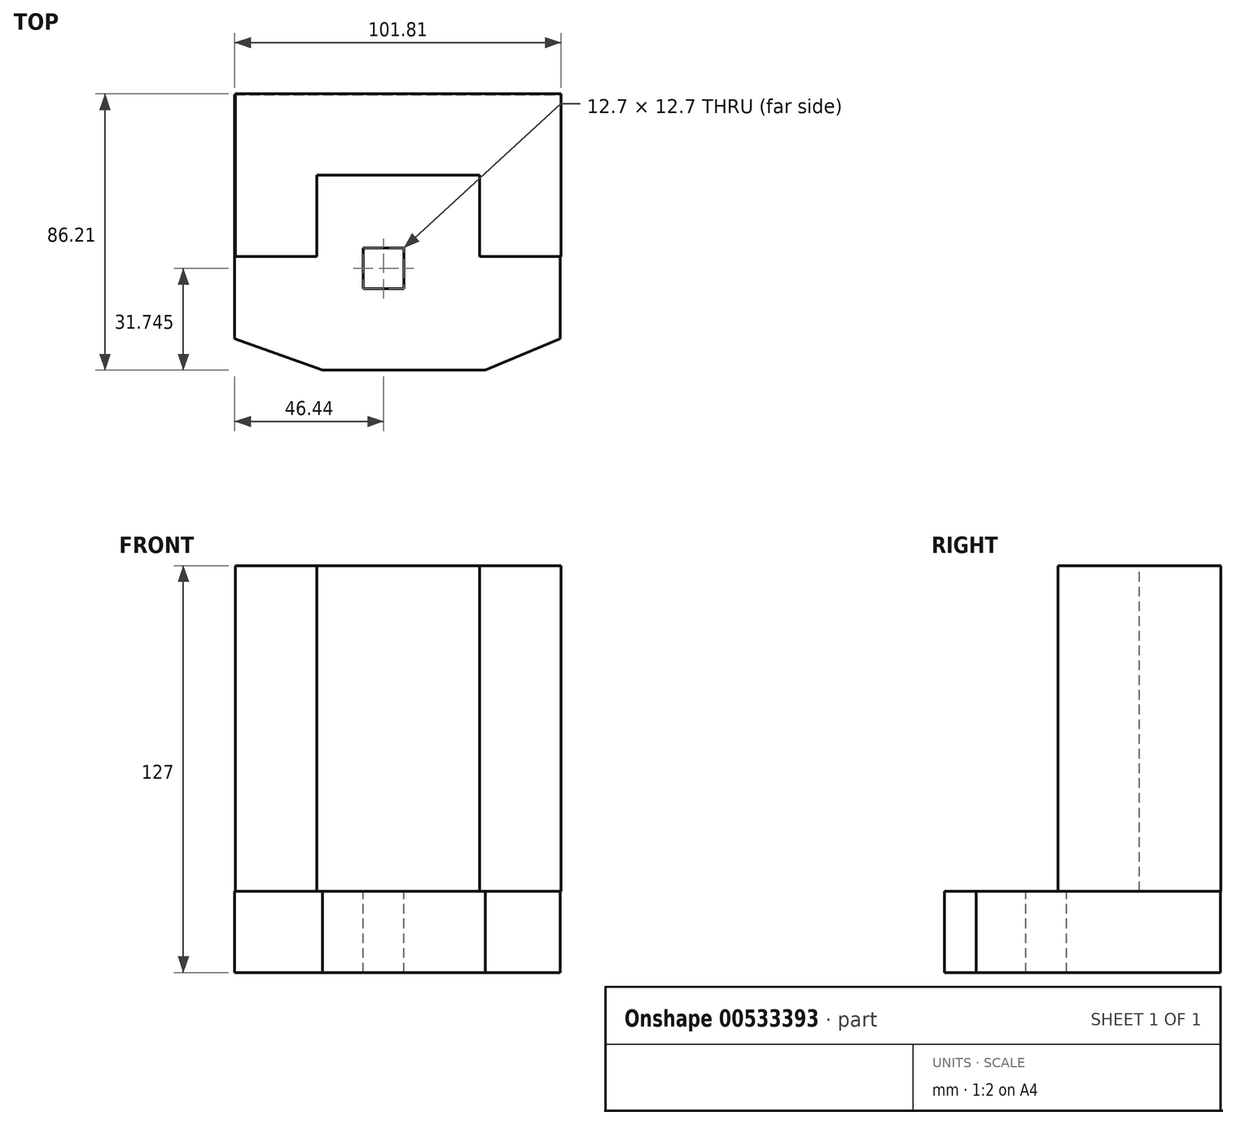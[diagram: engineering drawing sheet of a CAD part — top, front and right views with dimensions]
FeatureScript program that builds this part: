
annotation { "Feature Type Name" : "Feature", "Feature Type Description" : "" }
export const myFeature = defineFeature(function(context is Context, id is Id, definition is map)
    precondition{}
    {
        {
            var Q0;
            Q0=qCreatedBy(makeId("Top.planeOp"),FACE);
            var sketch = newSketch(context, id + "F0", { "sketchPlane" : qUnion([Q0])});
            skLineSegment(sketch, "E0", {"start": v(-55.12, 52.17) * mm, "end": v(46.48, 52.17) * mm});
            skLineSegment(sketch, "E1", {"start": v(46.48, 52.17) * mm, "end": v(46.48, 1.37) * mm});
            skLineSegment(sketch, "E2", {"start": v(46.48, 1.37) * mm, "end": v(21.08, 1.37) * mm});
            skLineSegment(sketch, "E3", {"start": v(21.08, 1.37) * mm, "end": v(21.08, 26.77) * mm});
            skLineSegment(sketch, "E4", {"start": v(21.08, 26.77) * mm, "end": v(-29.72, 26.77) * mm});
            skLineSegment(sketch, "E5", {"start": v(-29.72, 26.77) * mm, "end": v(-29.72, 1.37) * mm});
            skLineSegment(sketch, "E6", {"start": v(-29.72, 1.37) * mm, "end": v(-55.12, 1.37) * mm});
            skLineSegment(sketch, "E7", {"start": v(-55.12, 1.37) * mm, "end": v(-55.12, 52.17) * mm});
            skSolve(sketch);
        }
        {
            var Q0;
            Q0=makeQuery(id+"F0.imprint","IMPRINT",FACE,{"disambiguationData":[TD([[makeQuery(id+"F0.imprint","IMPRINT",EDGE,{"derivedFrom":sQuery(id+"F0.wireOp",EDGE,"E0")}),-1.0]])]});
            extrude(context, id + "F1", {"entities" : qUnion([Q0]), "oppositeDirection" : true, "depth" : 101.6 * mm, "offsetDistance" : 25.4 * mm});
        }
        {
            var Q0;
            Q0=makeQuery(id+"F1.opExtrude","SWEPT_BODY",BODY,{"disambiguationData":[OSD([sQuery(id+"F0.wireOp",EDGE,"E0"),sQuery(id+"F0.wireOp",EDGE,"E1"),sQuery(id+"F0.wireOp",EDGE,"E2"),sQuery(id+"F0.wireOp",EDGE,"E3"),sQuery(id+"F0.wireOp",EDGE,"E4"),sQuery(id+"F0.wireOp",EDGE,"E5"),sQuery(id+"F0.wireOp",EDGE,"E6"),sQuery(id+"F0.wireOp",EDGE,"E7")])]});
            transform(context, id + "F2", {"entities" : qUnion([Q0]), "transformType" : TransformType.TRANSLATION_3D, "dx" : 0 * mm, "dy" : 0 * mm, "dz" : 324.36 * mm, "makeCopy" : false});
        }
        {
            var Q0;
            Q0=qCreatedBy(makeId("Top.planeOp"),FACE);
            var sketch = newSketch(context, id + "F3", { "sketchPlane" : qUnion([Q0])});
            skLineSegment(sketch, "E8", {"start": v(-27.4, 8.84) * mm, "end": v(74.2, 8.84) * mm});
            skLineSegment(sketch, "E9", {"start": v(74.2, 8.84) * mm, "end": v(74.2, -67.36) * mm});
            skLineSegment(sketch, "E10", {"start": v(74.2, -67.36) * mm, "end": v(50.8, -77.22) * mm});
            skLineSegment(sketch, "E11", {"start": v(50.8, -77.22) * mm, "end": v(0, -77.22) * mm});
            skLineSegment(sketch, "E12", {"start": v(-27.4, 8.84) * mm, "end": v(-27.4, -67.36) * mm});
            skLineSegment(sketch, "E13", {"start": v(-27.4, -67.36) * mm, "end": v(0, -77.22) * mm});
            skSolve(sketch);
        }
        {
            var Q0;
            Q0=makeQuery(id+"F3.imprint","IMPRINT",FACE,{"disambiguationData":[TD([[makeQuery(id+"F3.imprint","IMPRINT",EDGE,{"derivedFrom":sQuery(id+"F3.wireOp",EDGE,"E8")}),-1.0]])]});
            extrude(context, id + "F4", {"entities" : qUnion([Q0]), "depth" : 25.4 * mm, "offsetDistance" : 25.4 * mm});
        }
        {
            var Q0;
            Q0=makeQuery(id+"F4.opExtrude","CAP_FACE",FACE,{"disambiguationData":[OSD([sQuery(id+"F3.wireOp",EDGE,"E8"),sQuery(id+"F3.wireOp",EDGE,"E9"),sQuery(id+"F3.wireOp",EDGE,"E10"),sQuery(id+"F3.wireOp",EDGE,"E11"),sQuery(id+"F3.wireOp",EDGE,"E12"),sQuery(id+"F3.wireOp",EDGE,"E13")])],"isStart":false});
            var sketch = newSketch(context, id + "F5", { "sketchPlane" : qUnion([Q0])});
            skLineSegment(sketch, "E14", {"start": v(25.4, -51.82) * mm, "end": v(38.1, -51.82) * mm});
            skLineSegment(sketch, "E15", {"start": v(38.1, -51.82) * mm, "end": v(38.1, -64.52) * mm});
            skLineSegment(sketch, "E16", {"start": v(38.1, -64.52) * mm, "end": v(25.4, -64.52) * mm});
            skLineSegment(sketch, "E17", {"start": v(25.4, -51.82) * mm, "end": v(25.4, -64.52) * mm});
            skSolve(sketch);
        }
        {
            var Q0;
            Q0=makeQuery(id+"F5.imprint","IMPRINT",FACE,{"disambiguationData":[TD([[makeQuery(id+"F5.imprint","IMPRINT",EDGE,{"derivedFrom":sQuery(id+"F5.wireOp",EDGE,"E14")}),-1.0]])]});
            extrude(context, id + "F6", {"entities" : qUnion([Q0]), "operationType" : NewBodyOperationType.ADD, "oppositeDirection" : true, "depth" : 25.4 * mm, "offsetDistance" : 25.4 * mm});
        }
        {
            var Q0;
            Q0=makeQuery(id+"F1.opExtrude","SWEPT_BODY",BODY,{"disambiguationData":[OSD([sQuery(id+"F0.wireOp",EDGE,"E0"),sQuery(id+"F0.wireOp",EDGE,"E1"),sQuery(id+"F0.wireOp",EDGE,"E2"),sQuery(id+"F0.wireOp",EDGE,"E3"),sQuery(id+"F0.wireOp",EDGE,"E4"),sQuery(id+"F0.wireOp",EDGE,"E5"),sQuery(id+"F0.wireOp",EDGE,"E6"),sQuery(id+"F0.wireOp",EDGE,"E7")])]});
            transform(context, id + "F7", {"entities" : qUnion([Q0]), "transformType" : TransformType.TRANSLATION_3D, "dx" : 27.94 * mm, "dy" : -43.18 * mm, "dz" : -197.36 * mm, "makeCopy" : false});
        }
        {
            var Q0;
            Q0=makeQuery(id+"F4.opExtrude","CAP_FACE",FACE,{"disambiguationData":[OSD([sQuery(id+"F3.wireOp",EDGE,"E8"),sQuery(id+"F3.wireOp",EDGE,"E9"),sQuery(id+"F3.wireOp",EDGE,"E10"),sQuery(id+"F3.wireOp",EDGE,"E11"),sQuery(id+"F3.wireOp",EDGE,"E12"),sQuery(id+"F3.wireOp",EDGE,"E13")])],"isStart":false});
            var sketch = newSketch(context, id + "F8", { "sketchPlane" : qUnion([Q0])});
            skLineSegment(sketch, "E18", {"start": v(25.4, -51.82) * mm, "end": v(12.7, -51.82) * mm});
            skLineSegment(sketch, "E19", {"start": v(12.7, -51.82) * mm, "end": v(12.7, -39.12) * mm});
            skLineSegment(sketch, "E20", {"start": v(12.7, -39.12) * mm, "end": v(25.4, -39.12) * mm});
            skLineSegment(sketch, "E21", {"start": v(25.4, -39.12) * mm, "end": v(25.4, -51.82) * mm});
            skSolve(sketch);
        }
        {
            var Q0;
            Q0=makeQuery(id+"F8.imprint","IMPRINT",FACE,{"disambiguationData":[TD([[makeQuery(id+"F8.imprint","IMPRINT",EDGE,{"derivedFrom":sQuery(id+"F8.wireOp",EDGE,"E18")}),-1.0]])]});
            extrude(context, id + "F9", {"entities" : qUnion([Q0]), "operationType" : NewBodyOperationType.REMOVE, "oppositeDirection" : true, "depth" : 25.4 * mm, "offsetDistance" : 25.4 * mm});
        }
    });
